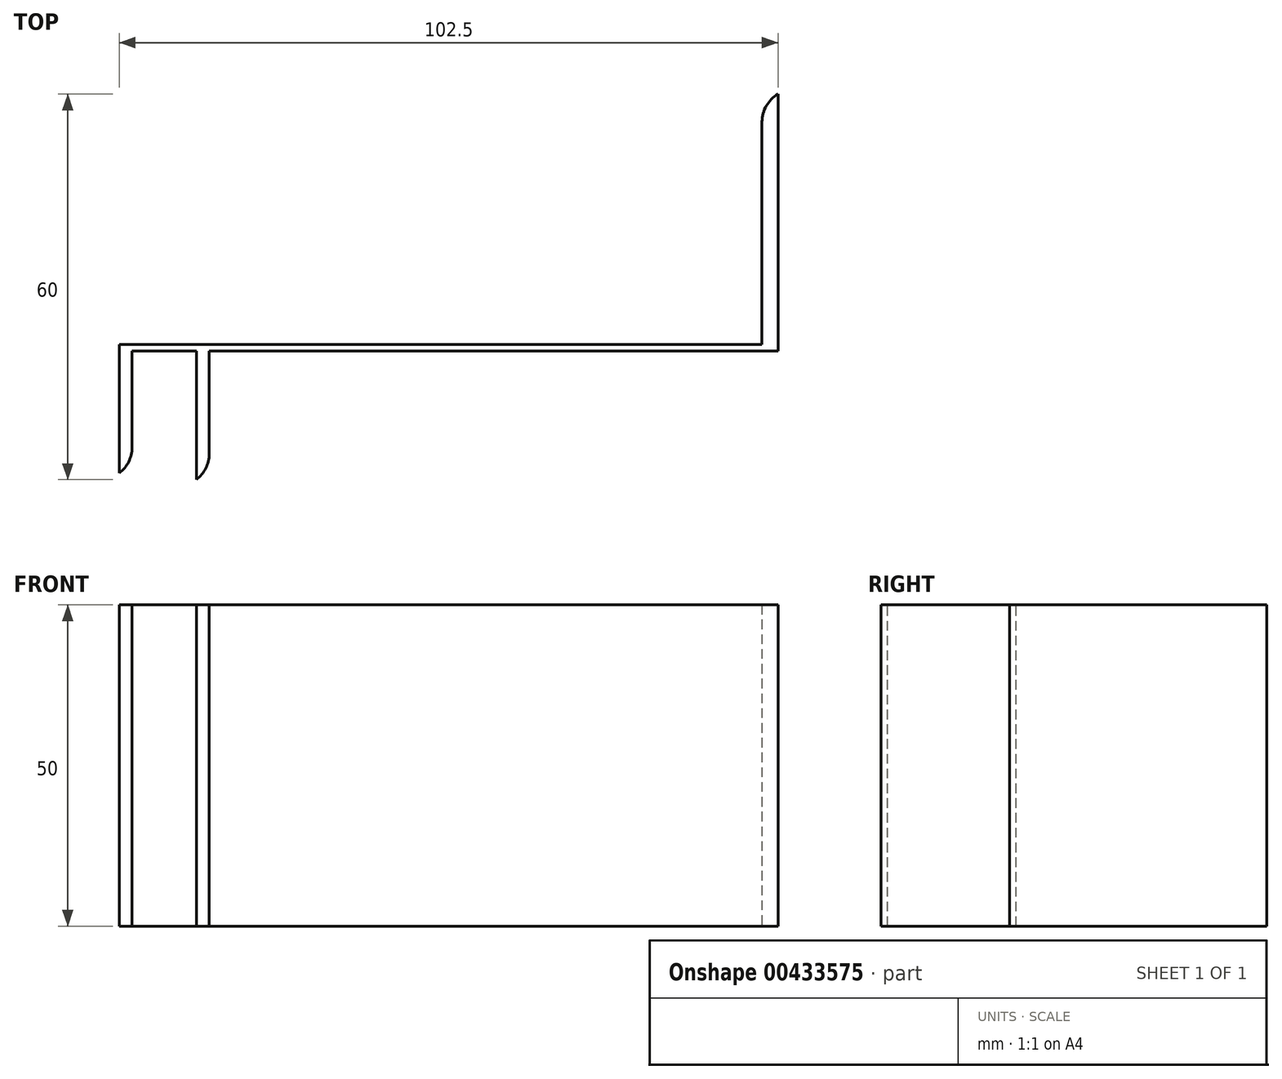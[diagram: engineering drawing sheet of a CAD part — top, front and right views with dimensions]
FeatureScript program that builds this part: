
annotation { "Feature Type Name" : "Feature", "Feature Type Description" : "" }
export const myFeature = defineFeature(function(context is Context, id is Id, definition is map)
    precondition{}
    {
        {
            var Q0;
            Q0=qCreatedBy(makeId("Top.planeOp"),FACE);
            var sketch = newSketch(context, id + "F0", { "sketchPlane" : qUnion([Q0])});
            skLineSegment(sketch, "E0.bottom", {"start": v(-34.31, -8.75) * mm, "end": v(15.69, -8.75) * mm});
            skLineSegment(sketch, "E0.top", {"start": v(-34.31, -48.75) * mm, "end": v(15.69, -48.75) * mm});
            skLineSegment(sketch, "E0.left", {"start": v(-34.31, -8.75) * mm, "end": v(-34.31, -48.75) * mm});
            skLineSegment(sketch, "E0.right", {"start": v(15.69, -8.75) * mm, "end": v(15.69, -48.75) * mm});
            skSolve(sketch);
        }
        {
            var Q0;
            Q0=makeQuery(id+"F0.imprint","IMPRINT",FACE,{"disambiguationData":[TD([[makeQuery(id+"F0.imprint","IMPRINT",EDGE,{"derivedFrom":sQuery(id+"F0.wireOp",EDGE,"E0.bottom")}),-1.0]])]});
            extrude(context, id + "F1", {"entities" : qUnion([Q0]), "depth" : 2.5 * mm});
        }
        {
            var Q0;
            Q0=makeQuery(id+"F1.opExtrude","CAP_FACE",FACE,{"disambiguationData":[OSD([sQuery(id+"F0.wireOp",EDGE,"E0.bottom"),sQuery(id+"F0.wireOp",EDGE,"E0.top"),sQuery(id+"F0.wireOp",EDGE,"E0.left"),sQuery(id+"F0.wireOp",EDGE,"E0.right")])],"isStart":false});
            var sketch = newSketch(context, id + "F2", { "sketchPlane" : qUnion([Q0])});
            skLineSegment(sketch, "E1.bottom", {"start": v(-34.31, -47.75) * mm, "end": v(15.69, -47.75) * mm});
            skLineSegment(sketch, "E1.top", {"start": v(-34.31, -48.75) * mm, "end": v(15.69, -48.75) * mm});
            skLineSegment(sketch, "E1.left", {"start": v(-34.31, -47.75) * mm, "end": v(-34.31, -48.75) * mm});
            skLineSegment(sketch, "E1.right", {"start": v(15.69, -47.75) * mm, "end": v(15.69, -48.75) * mm});
            skSolve(sketch);
        }
        {
            var Q0;
            Q0=makeQuery(id+"F2.imprint","IMPRINT",FACE,{"disambiguationData":[TD([[makeQuery(id+"F2.imprint","IMPRINT",EDGE,{"derivedFrom":sQuery(id+"F2.wireOp",EDGE,"E1.bottom")}),-1.0]])]});
            extrude(context, id + "F3", {"entities" : qUnion([Q0]), "operationType" : NewBodyOperationType.ADD, "depth" : 100 * mm});
        }
        {
            var Q0;
            Q0=makeQuery(id+"F1.opExtrude","CAP_EDGE",EDGE,{"disambiguationData":[OSD([sQuery(id+"F0.wireOp",EDGE,"E0.bottom")])],"isStart":false});
            fillet(context, id + "F4", {"entities" : qUnion([Q0]), "radius" : 5 * mm, "tangentPropagation" : true, "allowEdgeOverflow" : false});
        }
        {
            var Q0;
            Q0=makeQuery(id+"F1.opExtrude","SWEPT_BODY",BODY,{"disambiguationData":[OSD([sQuery(id+"F0.wireOp",EDGE,"E0.bottom"),sQuery(id+"F0.wireOp",EDGE,"E0.top"),sQuery(id+"F0.wireOp",EDGE,"E0.left"),sQuery(id+"F0.wireOp",EDGE,"E0.right")])]});
            var Q1;
            Q1=makeQuery(id+"F1.opExtrude","CAP_EDGE",EDGE,{"disambiguationData":[OSD([sQuery(id+"F0.wireOp",EDGE,"E0.right")])],"isStart":true});
            transform(context, id + "F5", {"entities" : qUnion([Q0]), "transformType" : TransformType.ROTATION, "transformAxis" : qUnion([Q1]), "angle" : 90 * degree, "makeCopy" : false});
        }
        {
            var Q0;
            Q0=makeQuery(id+"F1.opExtrude","SWEPT_BODY",BODY,{"disambiguationData":[OSD([sQuery(id+"F0.wireOp",EDGE,"E0.bottom"),sQuery(id+"F0.wireOp",EDGE,"E0.top"),sQuery(id+"F0.wireOp",EDGE,"E0.left"),sQuery(id+"F0.wireOp",EDGE,"E0.right")])]});
            transform(context, id + "F6", {"entities" : qUnion([Q0]), "transformType" : TransformType.TRANSLATION_3D, "dx" : 25.7 * mm, "dy" : 0 * mm, "dz" : 0 * mm, "makeCopy" : false});
        }
        {
            var Q0;
            Q0=makeQuery(id+"F3.opExtrude","SWEPT_FACE",FACE,{"disambiguationData":[OSD([sQuery(id+"F2.wireOp",EDGE,"E1.bottom")])]});
            var sketch = newSketch(context, id + "F7", { "sketchPlane" : qUnion([Q0])});
            skLineSegment(sketch, "E2.bottom", {"start": v(61.11, 0) * mm, "end": v(59.11, 0) * mm});
            skLineSegment(sketch, "E2.top", {"start": v(61.11, -50) * mm, "end": v(59.11, -50) * mm});
            skLineSegment(sketch, "E2.left", {"start": v(61.11, 0) * mm, "end": v(61.11, -50) * mm});
            skLineSegment(sketch, "E2.right", {"start": v(59.11, 0) * mm, "end": v(59.11, -50) * mm});
            skSolve(sketch);
        }
        {
            var Q0;
            Q0=makeQuery(id+"F7.imprint","IMPRINT",FACE,{"disambiguationData":[TD([[makeQuery(id+"F7.imprint","IMPRINT",EDGE,{"derivedFrom":sQuery(id+"F7.wireOp",EDGE,"E2.bottom")}),1.0]])]});
            extrude(context, id + "F8", {"entities" : qUnion([Q0]), "operationType" : NewBodyOperationType.ADD, "oppositeDirection" : true, "depth" : 20 * mm});
        }
        {
            var Q0;
            Q0=makeQuery(id+"F8.opExtrude","CAP_EDGE",EDGE,{"disambiguationData":[OSD([sQuery(id+"F7.wireOp",EDGE,"E2.right")])],"isStart":false});
            fillet(context, id + "F9", {"entities" : qUnion([Q0]), "radius" : 5 * mm, "tangentPropagation" : true, "allowEdgeOverflow" : false});
        }
        {
            var Q0;
            Q0=makeQuery(id+"F3.opExtrude","SWEPT_FACE",FACE,{"disambiguationData":[OSD([sQuery(id+"F2.wireOp",EDGE,"E1.top")])]});
            var sketch = newSketch(context, id + "F10", { "sketchPlane" : qUnion([Q0])});
            skLineSegment(sketch, "E3.bottom", {"start": v(-49.11, 0) * mm, "end": v(-47.11, 0) * mm});
            skLineSegment(sketch, "E3.top", {"start": v(-49.11, -50) * mm, "end": v(-47.11, -50) * mm});
            skLineSegment(sketch, "E3.left", {"start": v(-49.11, 0) * mm, "end": v(-49.11, -50) * mm});
            skLineSegment(sketch, "E3.right", {"start": v(-47.11, 0) * mm, "end": v(-47.11, -50) * mm});
            skSolve(sketch);
        }
        {
            var Q0;
            Q0=makeQuery(id+"F10.imprint","IMPRINT",FACE,{"disambiguationData":[TD([[makeQuery(id+"F10.imprint","IMPRINT",EDGE,{"derivedFrom":sQuery(id+"F10.wireOp",EDGE,"E3.bottom")}),-1.0]])]});
            extrude(context, id + "F11", {"entities" : qUnion([Q0]), "operationType" : NewBodyOperationType.ADD, "depth" : 20 * mm});
        }
        {
            var Q0;
            Q0=makeQuery(id+"F11.opExtrude","CAP_EDGE",EDGE,{"disambiguationData":[OSD([sQuery(id+"F10.wireOp",EDGE,"E3.right")])],"isStart":false});
            fillet(context, id + "F12", {"entities" : qUnion([Q0]), "radius" : 5 * mm, "tangentPropagation" : true, "allowEdgeOverflow" : false});
        }
    });
